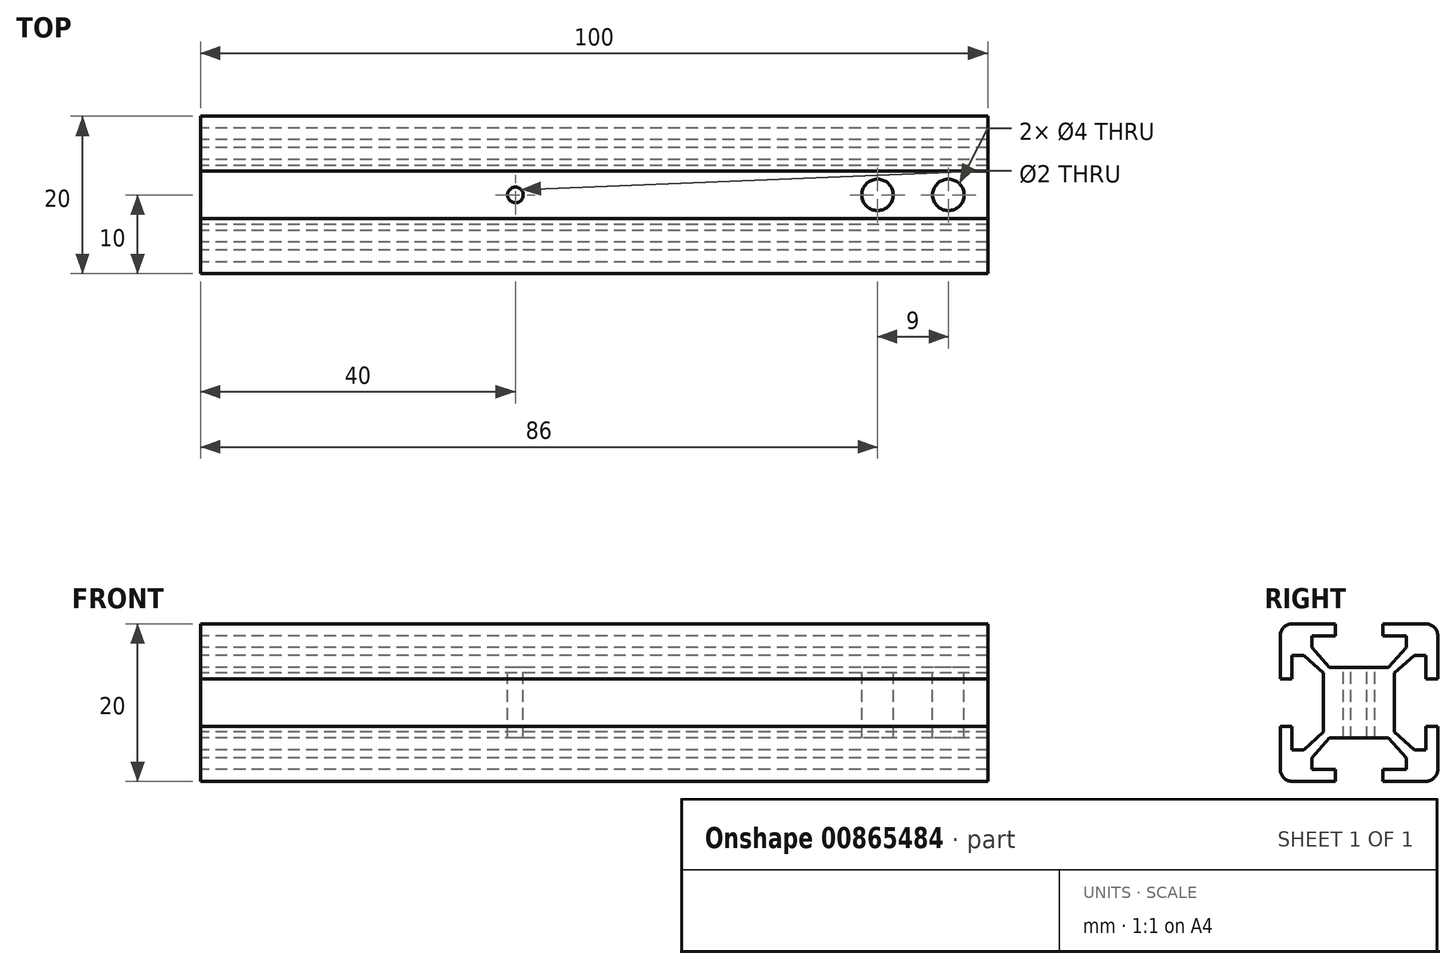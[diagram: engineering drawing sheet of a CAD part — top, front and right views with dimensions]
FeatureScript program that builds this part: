
annotation { "Feature Type Name" : "Feature", "Feature Type Description" : "" }
export const myFeature = defineFeature(function(context is Context, id is Id, definition is map)
    precondition{}
    {
        {
            var Q0;
            Q0=qCreatedBy(makeId("Right.planeOp"),FACE);
            var sketch = newSketch(context, id + "F0", { "sketchPlane" : qUnion([Q0])});
            skLineSegment(sketch, "E0.bottom", {"start": v(8.5, 10) * mm, "end": v(3, 10) * mm});
            skLineSegment(sketch, "E0.top", {"start": v(8.5, -10) * mm, "end": v(-8.5, -10) * mm});
            skLineSegment(sketch, "E0.left", {"start": v(10, 8.5) * mm, "end": v(10, 3) * mm});
            skLineSegment(sketch, "E0.right", {"start": v(-10, 8.5) * mm, "end": v(-10, 3) * mm});
            skPoint(sketch, "E0.middle", {"position": v(0, 0) * mm});
            skPoint(sketch, "E1.visualSharp", {"position": v(-10, 10) * mm});
            skArc(sketch, "E1.filletArc", {"start": v(-8.5, 10) * mm, "mid": v(-9.56, 9.56) * mm, "end": v(-10, 8.5) * mm});
            skPoint(sketch, "E2.visualSharp", {"position": v(10, 10) * mm});
            skArc(sketch, "E2.filletArc", {"start": v(10, 8.5) * mm, "mid": v(9.56, 9.56) * mm, "end": v(8.5, 10) * mm});
            skPoint(sketch, "E3.visualSharp", {"position": v(10, -10) * mm});
            skArc(sketch, "E3.filletArc", {"start": v(8.5, -10) * mm, "mid": v(9.56, -9.56) * mm, "end": v(10, -8.5) * mm});
            skPoint(sketch, "E4.visualSharp", {"position": v(-10, -10) * mm});
            skArc(sketch, "E4.filletArc", {"start": v(-10, -8.5) * mm, "mid": v(-9.56, -9.56) * mm, "end": v(-8.5, -10) * mm});
            skLineSegment(sketch, "E5", {"start": v(-3, 10) * mm, "end": v(-3, 8.5) * mm});
            skLineSegment(sketch, "E6", {"start": v(-3, 8.5) * mm, "end": v(-6, 8.5) * mm});
            skLineSegment(sketch, "E7", {"start": v(-6, 8.5) * mm, "end": v(-6, 7) * mm});
            skLineSegment(sketch, "E8", {"start": v(-6, 7) * mm, "end": v(-3.75, 4.5) * mm});
            skLineSegment(sketch, "E9", {"start": v(-3.75, 4.5) * mm, "end": v(0, 4.5) * mm});
            skLineSegment(sketch, "E10.MirrorCS", {"start": v(3, 10) * mm, "end": v(3, 8.5) * mm});
            skLineSegment(sketch, "E11.MirrorCS", {"start": v(3, 8.5) * mm, "end": v(6, 8.5) * mm});
            skLineSegment(sketch, "E12.MirrorCS", {"start": v(6, 8.5) * mm, "end": v(6, 7) * mm});
            skLineSegment(sketch, "E13.MirrorCS", {"start": v(6, 7) * mm, "end": v(3.75, 4.5) * mm});
            skLineSegment(sketch, "E14.MirrorCS", {"start": v(3.75, 4.5) * mm, "end": v(0, 4.5) * mm});
            skLineSegment(sketch, "E15.trimOffspring", {"start": v(-3, 10) * mm, "end": v(-8.5, 10) * mm});
            skLineSegment(sketch, "E16.1.0", {"start": v(-8.5, -3) * mm, "end": v(-8.5, -6) * mm});
            skLineSegment(sketch, "E16.1.1", {"start": v(-8.5, -6) * mm, "end": v(-7, -6) * mm});
            skLineSegment(sketch, "E16.1.2", {"start": v(-7, -6) * mm, "end": v(-4.5, -3.75) * mm});
            skLineSegment(sketch, "E16.1.3", {"start": v(-4.5, -3.75) * mm, "end": v(-4.5, 0) * mm});
            skLineSegment(sketch, "E16.1.4", {"start": v(-4.5, 3.75) * mm, "end": v(-4.5, 0) * mm});
            skLineSegment(sketch, "E16.1.5", {"start": v(-7, 6) * mm, "end": v(-4.5, 3.75) * mm});
            skLineSegment(sketch, "E16.1.6", {"start": v(-8.5, 6) * mm, "end": v(-7, 6) * mm});
            skLineSegment(sketch, "E16.1.7", {"start": v(-8.5, 3) * mm, "end": v(-8.5, 6) * mm});
            skLineSegment(sketch, "E16.1.8", {"start": v(-10, 3) * mm, "end": v(-8.5, 3) * mm});
            skLineSegment(sketch, "E16.1.9", {"start": v(-10, -3) * mm, "end": v(-8.5, -3) * mm});
            skLineSegment(sketch, "E16.2.0", {"start": v(3, -8.5) * mm, "end": v(6, -8.5) * mm});
            skLineSegment(sketch, "E16.2.1", {"start": v(6, -8.5) * mm, "end": v(6, -7) * mm});
            skLineSegment(sketch, "E16.2.2", {"start": v(6, -7) * mm, "end": v(3.75, -4.5) * mm});
            skLineSegment(sketch, "E16.2.3", {"start": v(3.75, -4.5) * mm, "end": v(0, -4.5) * mm});
            skLineSegment(sketch, "E16.2.4", {"start": v(-3.75, -4.5) * mm, "end": v(0, -4.5) * mm});
            skLineSegment(sketch, "E16.2.5", {"start": v(-6, -7) * mm, "end": v(-3.75, -4.5) * mm});
            skLineSegment(sketch, "E16.2.6", {"start": v(-6, -8.5) * mm, "end": v(-6, -7) * mm});
            skLineSegment(sketch, "E16.2.7", {"start": v(-3, -8.5) * mm, "end": v(-6, -8.5) * mm});
            skLineSegment(sketch, "E16.2.8", {"start": v(-3, -10) * mm, "end": v(-3, -8.5) * mm});
            skLineSegment(sketch, "E16.2.9", {"start": v(3, -10) * mm, "end": v(3, -8.5) * mm});
            skLineSegment(sketch, "E16.3.0", {"start": v(8.5, 3) * mm, "end": v(8.5, 6) * mm});
            skLineSegment(sketch, "E16.3.1", {"start": v(8.5, 6) * mm, "end": v(7, 6) * mm});
            skLineSegment(sketch, "E16.3.2", {"start": v(7, 6) * mm, "end": v(4.5, 3.75) * mm});
            skLineSegment(sketch, "E16.3.3", {"start": v(4.5, 3.75) * mm, "end": v(4.5, 0) * mm});
            skLineSegment(sketch, "E16.3.4", {"start": v(4.5, -3.75) * mm, "end": v(4.5, 0) * mm});
            skLineSegment(sketch, "E16.3.5", {"start": v(7, -6) * mm, "end": v(4.5, -3.75) * mm});
            skLineSegment(sketch, "E16.3.6", {"start": v(8.5, -6) * mm, "end": v(7, -6) * mm});
            skLineSegment(sketch, "E16.3.7", {"start": v(8.5, -3) * mm, "end": v(8.5, -6) * mm});
            skLineSegment(sketch, "E16.3.8", {"start": v(10, -3) * mm, "end": v(8.5, -3) * mm});
            skLineSegment(sketch, "E16.3.9", {"start": v(10, 3) * mm, "end": v(8.5, 3) * mm});
            skLineSegment(sketch, "E17.trimOffspring", {"start": v(-10, -3) * mm, "end": v(-10, -8.5) * mm});
            skLineSegment(sketch, "E18.trimOffspring", {"start": v(10, -3) * mm, "end": v(10, -8.5) * mm});
            skSolve(sketch);
        }
        {
            var Q0;
            Q0=makeQuery(id+"F0.imprint","IMPRINT",FACE,{"disambiguationData":[TD([[makeQuery(id+"F0.imprint","IMPRINT",EDGE,{"derivedFrom":sQuery(id+"F0.wireOp",EDGE,"E0.bottom")}),1.0]])]});
            extrude(context, id + "F1", {"entities" : qUnion([Q0]), "depth" : 100 * mm, "offsetDistance" : 25 * mm});
        }
        {
            var Q0;
            Q0=makeQuery(id+"F1.opExtrude","SWEPT_FACE",FACE,{"disambiguationData":[OSD([sQuery(id+"F0.wireOp",EDGE,"E9"),sQuery(id+"F0.wireOp",EDGE,"E14.MirrorCS")])]});
            var sketch = newSketch(context, id + "F2", { "sketchPlane" : qUnion([Q0])});
            skCircle(sketch, "E19", {"center": v(86, 0) * mm, "radius": 2 * mm});
            skCircle(sketch, "E20", {"center": v(95, 0) * mm, "radius": 2 * mm});
            skCircle(sketch, "E21", {"center": v(40, 0) * mm, "radius": 1 * mm});
            skSolve(sketch);
        }
        {
            var Q0;
            Q0 = qSketchRegion(id + "F2", true);
            extrude(context, id + "F3", {"entities" : qUnion([Q0]), "operationType" : NewBodyOperationType.REMOVE, "endBound" : BoundingType.THROUGH_ALL, "oppositeDirection" : true, "depth" : 25 * mm, "offsetDistance" : 25 * mm});
        }
    });
